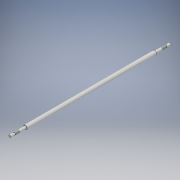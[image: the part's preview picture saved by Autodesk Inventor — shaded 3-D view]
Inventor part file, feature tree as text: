
AUTODESK INVENTOR PART (.ipt)
format: ipt  version: 2018 (Build 220112000, 112)  size: 109,568 bytes
history: native  units: mm
features: extrude x3, sketch x3, thread x2, mirror x1
ambient origin geometry x8: Origin, YZ Plane, XZ Plane, XY Plane, X Axis, Y Axis, Z Axis, Center Point
bodies: Solid1 (feature_tree)
feature tree (9):
  extrude  "Extrusion1"  Depth=464.0mm TaperAngle=0.0deg
  extrude  "Extrusion2"  Depth=40.0mm TaperAngle=0.0deg
  extrude  "Extrusion3"  Depth=15.0mm TaperAngle=0.0deg
  mirror  "Mirror2"
  thread  "Thread1"  [1 undecoded]
  thread  "Thread2"  [1 undecoded]
  sketch  "Sketch1"  dims[d0=14.0mm d1=464.0mm d2=0.0mm]
  sketch  "Sketch2"  dims[d3=9.0mm d4=40.0mm d5=0.0mm]
  sketch  "Sketch3"  dims[d6=8.0mm d7=15.0mm d8=0.0mm d9=17.0mm d10=0.0mm d11=17.0mm d12=0.0mm]
note: 2 required parameter values undecoded (feature->parameter linkage not recoverable at this tier; creation-order binding heuristic only, values carry confidence <= 0.55)
